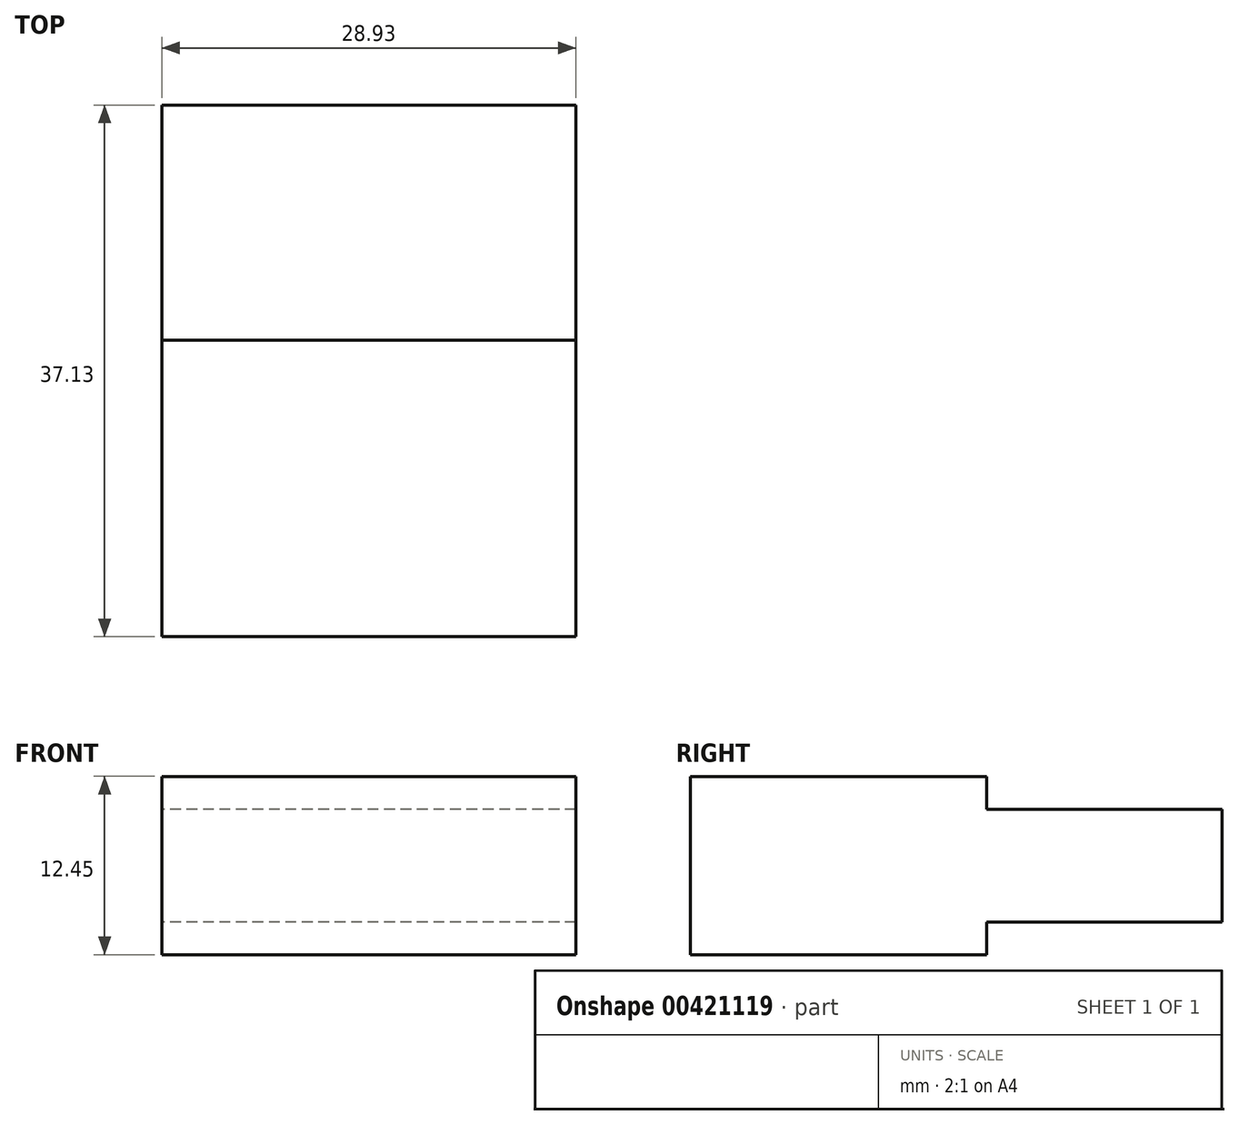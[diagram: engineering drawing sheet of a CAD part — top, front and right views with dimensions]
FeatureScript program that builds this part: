
annotation { "Feature Type Name" : "Feature", "Feature Type Description" : "" }
export const myFeature = defineFeature(function(context is Context, id is Id, definition is map)
    precondition{}
    {
        {
            var Q0;
            Q0=qCreatedBy(makeId("Right.planeOp"),FACE);
            var sketch = newSketch(context, id + "F0", { "sketchPlane" : qUnion([Q0])});
            skLineSegment(sketch, "E0.bottom", {"start": v(0, 0) * mm, "end": v(20.7, 0) * mm});
            skLineSegment(sketch, "E0.top", {"start": v(0, 12.45) * mm, "end": v(20.7, 12.45) * mm});
            skLineSegment(sketch, "E0.left", {"start": v(0, 0) * mm, "end": v(0, 12.45) * mm});
            skLineSegment(sketch, "E0.right", {"start": v(20.7, 0) * mm, "end": v(20.7, 2.29) * mm});
            skPoint(sketch, "E1.endSnap0", {"position": v(20.7, 6.22) * mm});
            skLineSegment(sketch, "E2", {"start": v(37.13, 6.22) * mm, "end": v(37.13, 10.16) * mm});
            skLineSegment(sketch, "E3", {"start": v(37.13, 10.16) * mm, "end": v(20.7, 10.16) * mm});
            skLineSegment(sketch, "E4.MirrorCS", {"start": v(37.13, 2.29) * mm, "end": v(20.7, 2.29) * mm});
            skLineSegment(sketch, "E5.MirrorCS", {"start": v(37.13, 6.22) * mm, "end": v(37.13, 2.29) * mm});
            skLineSegment(sketch, "E6.trimOffspring", {"start": v(20.7, 10.16) * mm, "end": v(20.7, 12.45) * mm});
            skSolve(sketch);
        }
        {
            var Q0;
            Q0 = qSketchRegion(id + "F0", true);
            extrude(context, id + "F1", {"entities" : qUnion([Q0]), "depth" : 28.93 * mm});
        }
    });
